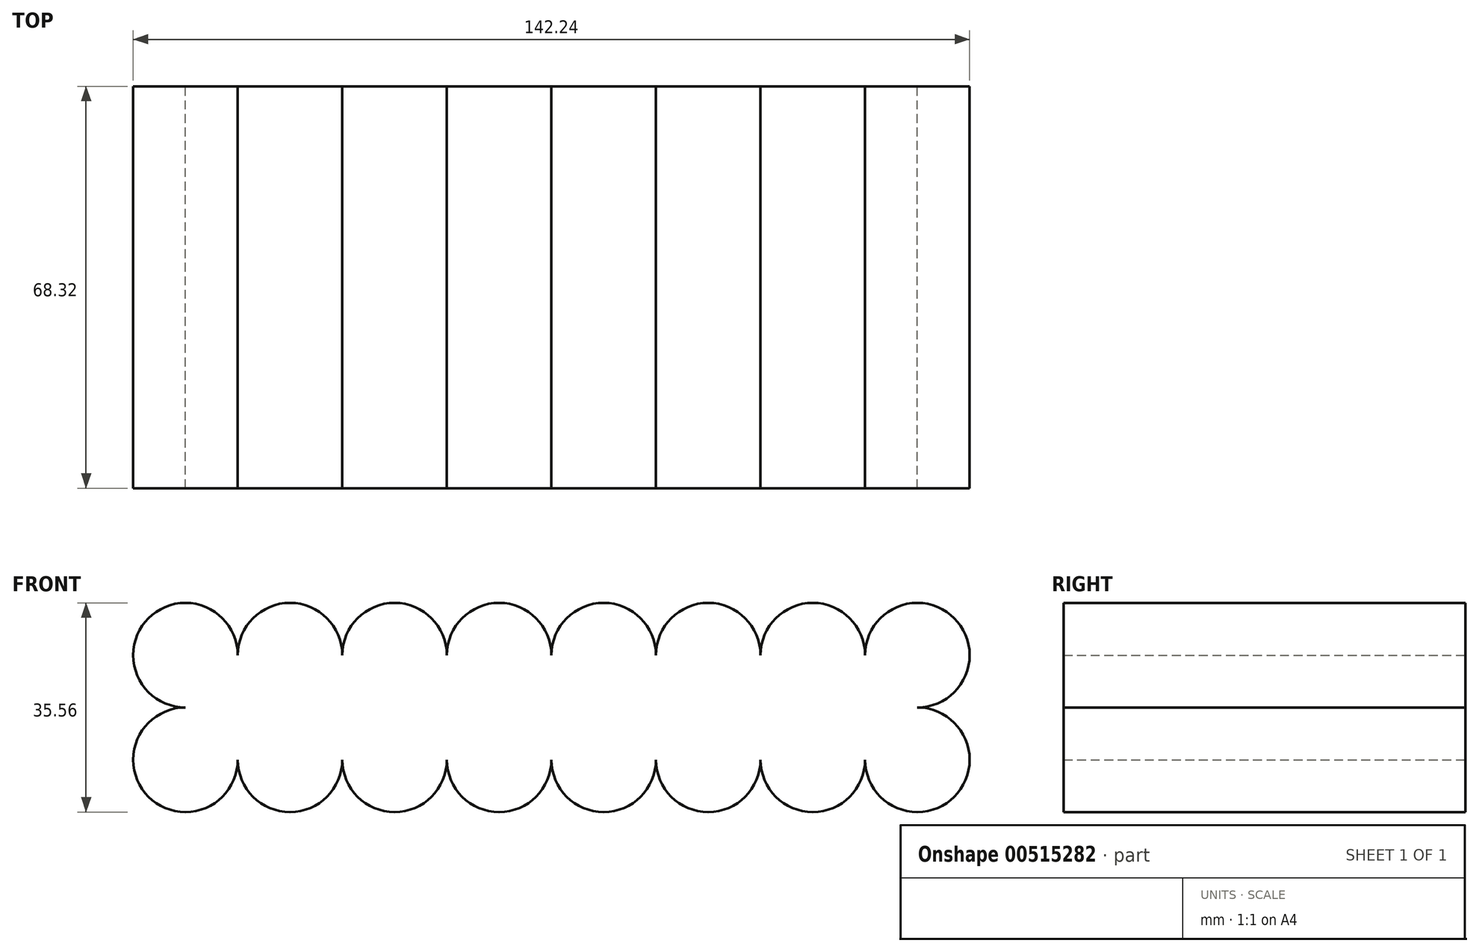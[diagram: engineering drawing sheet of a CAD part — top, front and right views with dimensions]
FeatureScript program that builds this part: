
annotation { "Feature Type Name" : "Feature", "Feature Type Description" : "" }
export const myFeature = defineFeature(function(context is Context, id is Id, definition is map)
    precondition{}
    {
        {
            var Q0;
            Q0=qCreatedBy(makeId("Front.planeOp"),FACE);
            var sketch = newSketch(context, id + "F0", { "sketchPlane" : qUnion([Q0])});
            skCircle(sketch, "E0", {"center": v(8.9, 8.9) * mm, "radius": 8.9 * mm});
            skCircle(sketch, "E1.0.1.0", {"center": v(8.9, 26.67) * mm, "radius": 8.9 * mm});
            skCircle(sketch, "E1.1.0.0", {"center": v(26.67, 8.9) * mm, "radius": 8.9 * mm});
            skCircle(sketch, "E1.1.1.0", {"center": v(26.67, 26.67) * mm, "radius": 8.9 * mm});
            skCircle(sketch, "E1.2.0.0", {"center": v(44.45, 8.9) * mm, "radius": 8.9 * mm});
            skCircle(sketch, "E1.2.1.0", {"center": v(44.45, 26.67) * mm, "radius": 8.9 * mm});
            skCircle(sketch, "E1.3.0.0", {"center": v(62.23, 8.9) * mm, "radius": 8.9 * mm});
            skCircle(sketch, "E1.3.1.0", {"center": v(62.23, 26.67) * mm, "radius": 8.9 * mm});
            skCircle(sketch, "E1.4.0.0", {"center": v(80, 8.9) * mm, "radius": 8.9 * mm});
            skCircle(sketch, "E1.4.1.0", {"center": v(80, 26.67) * mm, "radius": 8.9 * mm});
            skCircle(sketch, "E1.5.0.0", {"center": v(97.79, 8.9) * mm, "radius": 8.9 * mm});
            skCircle(sketch, "E1.5.1.0", {"center": v(97.79, 26.67) * mm, "radius": 8.9 * mm});
            skCircle(sketch, "E1.6.0.0", {"center": v(115.57, 8.9) * mm, "radius": 8.9 * mm});
            skCircle(sketch, "E1.6.1.0", {"center": v(115.57, 26.67) * mm, "radius": 8.9 * mm});
            skCircle(sketch, "E1.7.0.0", {"center": v(133.35, 8.9) * mm, "radius": 8.9 * mm});
            skCircle(sketch, "E1.7.1.0", {"center": v(133.35, 26.67) * mm, "radius": 8.9 * mm});
            skLineSegment(sketch, "E1.direction1", {"start": v(8.9, 8.9) * mm, "end": v(26.67, 8.9) * mm, "construction": true});
            skLineSegment(sketch, "E1.direction2", {"start": v(8.9, 8.9) * mm, "end": v(8.9, 26.67) * mm, "construction": true});
            skSolve(sketch);
        }
        {
            var Q0;
            Q0 = qSketchRegion(id + "F0", true);
            extrude(context, id + "F1", {"entities" : qUnion([Q0]), "endBound" : BoundingType.SYMMETRIC, "depth" : 68.33 * mm, "offsetDistance" : 25.4 * mm});
        }
    });
